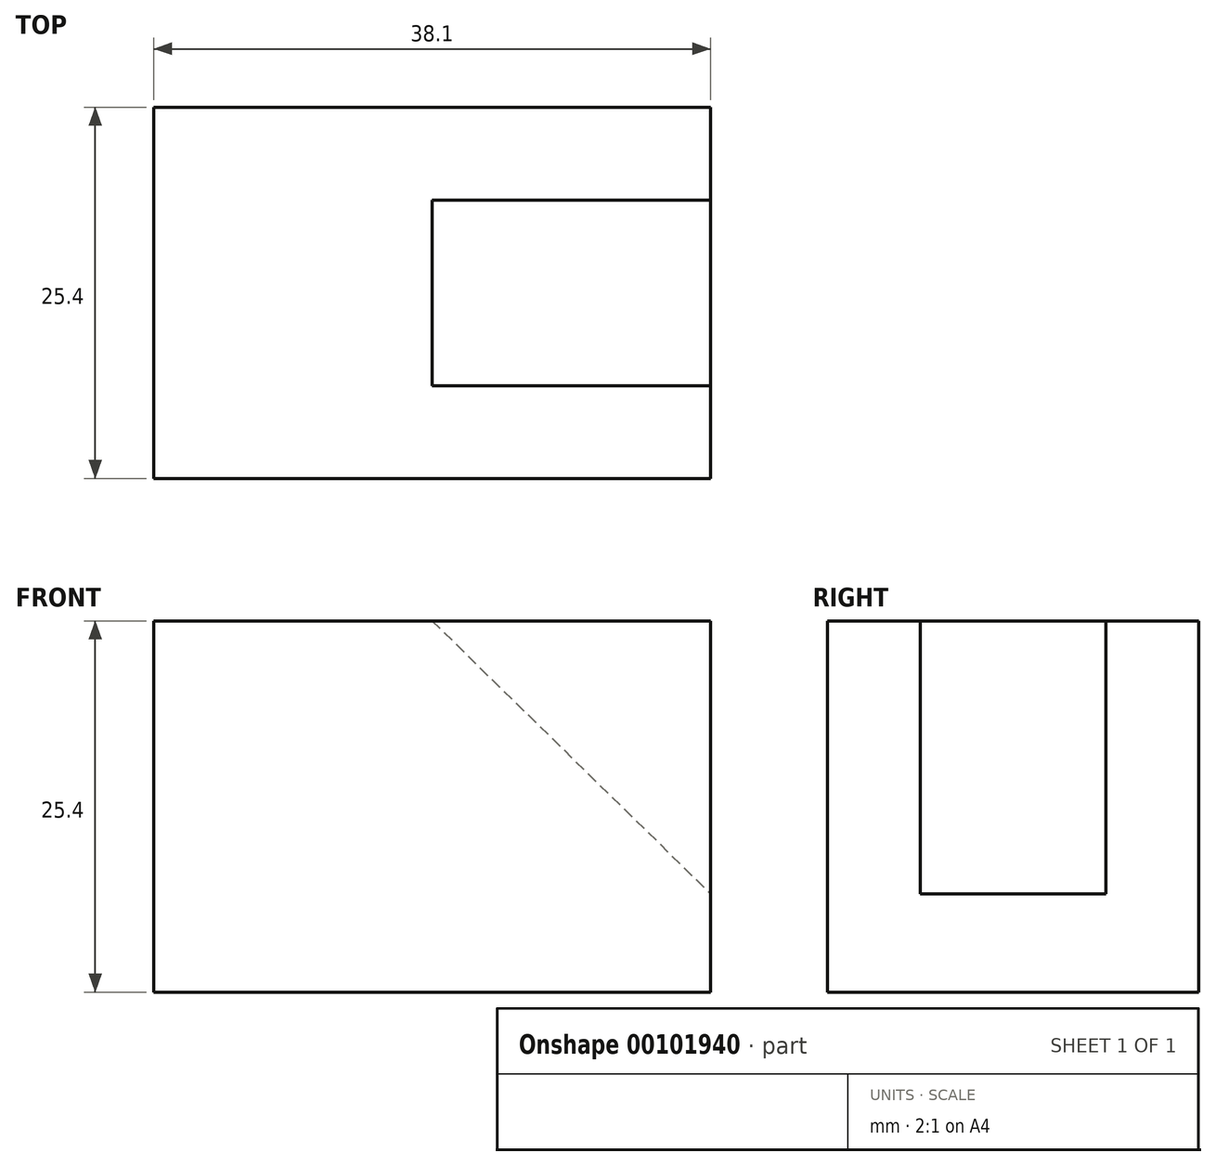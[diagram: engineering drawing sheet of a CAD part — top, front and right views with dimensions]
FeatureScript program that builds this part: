
annotation { "Feature Type Name" : "Feature", "Feature Type Description" : "" }
export const myFeature = defineFeature(function(context is Context, id is Id, definition is map)
    precondition{}
    {
        {
            var Q0;
            Q0=qCreatedBy(makeId("Front.planeOp"),FACE);
            var sketch = newSketch(context, id + "F0", { "sketchPlane" : qUnion([Q0])});
            skLineSegment(sketch, "E0.bottom", {"start": v(0, 0) * mm, "end": v(38.1, 0) * mm});
            skLineSegment(sketch, "E0.top", {"start": v(0, 25.4) * mm, "end": v(38.1, 25.4) * mm});
            skLineSegment(sketch, "E0.left", {"start": v(0, 0) * mm, "end": v(0, 25.4) * mm});
            skLineSegment(sketch, "E0.right", {"start": v(38.1, 0) * mm, "end": v(38.1, 25.4) * mm});
            skSolve(sketch);
        }
        {
            var Q0;
            Q0 = qSketchRegion(id + "F0", true);
            extrude(context, id + "F1", {"entities" : qUnion([Q0]), "endBound" : BoundingType.SYMMETRIC, "depth" : 25.4 * mm});
        }
        {
            var Q0;
            Q0=makeQuery(id+"F1.opExtrude","CAP_FACE",FACE,{"disambiguationData":[OSD([sQuery(id+"F0.wireOp",EDGE,"E0.bottom"),sQuery(id+"F0.wireOp",EDGE,"E0.top"),sQuery(id+"F0.wireOp",EDGE,"E0.left"),sQuery(id+"F0.wireOp",EDGE,"E0.right")])],"isStart":false});
            var sketch = newSketch(context, id + "F2", { "sketchPlane" : qUnion([Q0])});
            skLineSegment(sketch, "E1", {"start": v(19.05, 25.4) * mm, "end": v(38.1, 6.73) * mm});
            skSolve(sketch);
        }
        {
            var Q0;
            {var subQ0=sQuery(id+"F2.wireOp",EDGE,"E1");Q0=makeQuery(id+"F2.imprint","IMPRINT",FACE,{"disambiguationData":[TD([[makeQuery(id+"F2.imprint","IMPRINT",EDGE,{"derivedFrom":subQ0}),1.0]])]});}
            extrude(context, id + "F3", {"entities" : qUnion([Q0]), "operationType" : NewBodyOperationType.REMOVE, "oppositeDirection" : true, "depth" : 19.05 * mm, "hasSecondDirection" : true, "secondDirectionOppositeDirection" : true, "secondDirectionDepth" : 6.35 * mm});
        }
    });
